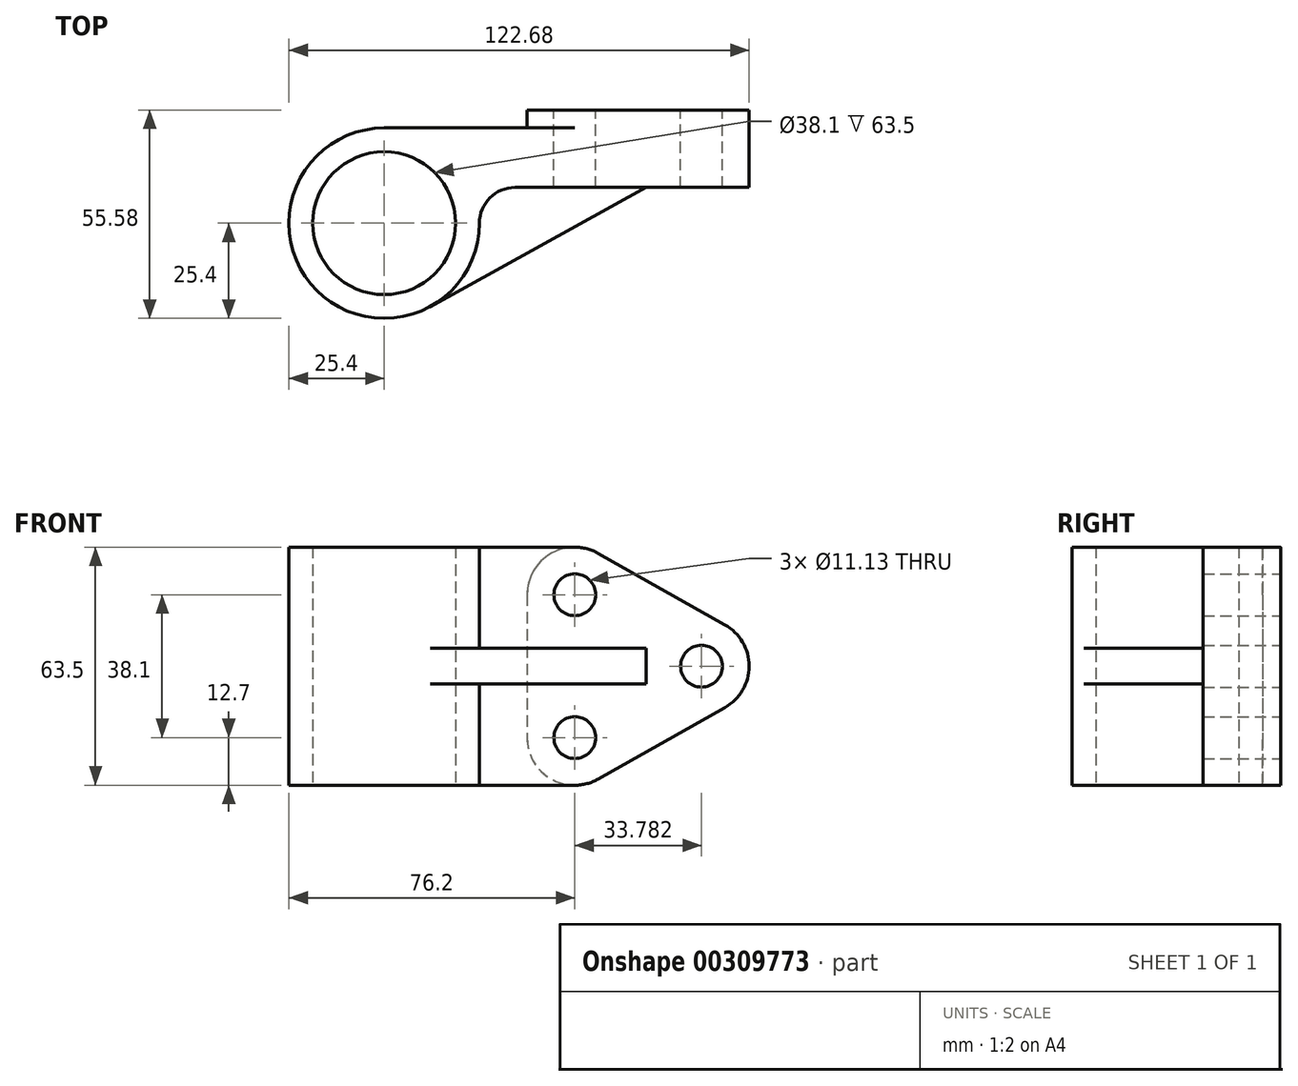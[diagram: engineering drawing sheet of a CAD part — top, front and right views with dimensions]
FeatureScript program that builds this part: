
annotation { "Feature Type Name" : "Feature", "Feature Type Description" : "" }
export const myFeature = defineFeature(function(context is Context, id is Id, definition is map)
    precondition{}
    {
        {
            var Q0;
            Q0=qCreatedBy(makeId("Top.planeOp"),FACE);
            var sketch = newSketch(context, id + "F0", { "sketchPlane" : qUnion([Q0])});
            skCircle(sketch, "E0", {"center": v(0, 0) * mm, "radius": 19.05 * mm});
            skLineSegment(sketch, "E1", {"start": v(0, 0) * mm, "end": v(25.4, 0) * mm});
            skLineSegment(sketch, "E2", {"start": v(34.92, 9.52) * mm, "end": v(84.58, 9.52) * mm});
            skLineSegment(sketch, "E3", {"start": v(0, 25.4) * mm, "end": v(50.8, 25.4) * mm});
            skLineSegment(sketch, "E4", {"start": v(50.8, 25.4) * mm, "end": v(50.8, 30.18) * mm});
            skLineSegment(sketch, "E5", {"start": v(50.8, 30.18) * mm, "end": v(84.58, 30.18) * mm});
            skLineSegment(sketch, "E6", {"start": v(84.58, 30.18) * mm, "end": v(84.58, 9.52) * mm});
            skArc(sketch, "E7", {"start": v(0, 25.4) * mm, "mid": v(-17.96, -17.96) * mm, "end": v(25.4, 0) * mm});
            skArc(sketch, "E8", {"start": v(34.92, 9.53) * mm, "mid": v(28.19, 6.74) * mm, "end": v(25.4, 0) * mm});
            skLineSegment(sketch, "E9", {"start": v(12.27, -22.24) * mm, "end": v(69.85, 9.52) * mm});
            skSolve(sketch);
        }
        {
            var Q0;
            Q0=makeQuery(id+"F0.imprint","IMPRINT",FACE,{"disambiguationData":[TD([[makeQuery(id+"F0.imprint","IMPRINT",EDGE,{"derivedFrom":sQuery(id+"F0.wireOp",EDGE,"E0")}),-1.0]])]});
            extrude(context, id + "F1", {"entities" : qUnion([Q0]), "endBound" : BoundingType.SYMMETRIC, "depth" : 63.5 * mm});
        }
        {
            var Q0;
            {var subQ0=sQuery(id+"F0.wireOp",EDGE,"E8");Q0=makeQuery(id+"F0.imprint","IMPRINT",FACE,{"disambiguationData":[TD([[makeQuery(id+"F0.imprint","IMPRINT",EDGE,{"derivedFrom":subQ0}),1.0]])]});}
            extrude(context, id + "F2", {"entities" : qUnion([Q0]), "operationType" : NewBodyOperationType.ADD, "endBound" : BoundingType.SYMMETRIC, "depth" : 9.52 * mm});
        }
        {
            var Q0;
            Q0=makeQuery(id+"F1.opExtrude","SWEPT_FACE",FACE,{"disambiguationData":[OSD([sQuery(id+"F0.wireOp",EDGE,"E5")])]});
            var sketch = newSketch(context, id + "F3", { "sketchPlane" : qUnion([Q0])});
            skSolve(sketch);
        }
        {
            var Q0;
            {var subQ0=sQuery(id+"F0.wireOp",EDGE,"E5");Q0=makeQuery(id+"F3.imprint","IMPRINT",FACE,{"disambiguationData":[TD([[makeQuery(id+"F3.imprint","IMPRINT",EDGE,{"derivedFrom":makeQuery(id+"F1.opExtrude","CAP_EDGE",EDGE,{"disambiguationData":[OSD([subQ0])],"isStart":true})}),-1.0]])]});}
            var sketch = newSketch(context, id + "F4", { "sketchPlane" : qUnion([Q0])});
            skCircle(sketch, "E10", {"center": v(-50.8, 19.05) * mm, "radius": 5.56 * mm});
            skCircle(sketch, "E11", {"center": v(-50.8, -19.05) * mm, "radius": 5.56 * mm});
            skCircle(sketch, "E12", {"center": v(-84.58, 0) * mm, "radius": 5.56 * mm});
            skLineSegment(sketch, "E13", {"start": v(-38.1, 19.05) * mm, "end": v(-38.1, -19.05) * mm});
            skArc(sketch, "E14", {"start": v(-38.1, 19.05) * mm, "mid": v(-44.4, 30.02) * mm, "end": v(-57.04, 30.11) * mm});
            skArc(sketch, "E15", {"start": v(-57.04, -30.11) * mm, "mid": v(-44.4, -30.02) * mm, "end": v(-38.1, -19.05) * mm});
            skLineSegment(sketch, "E16", {"start": v(-57.04, -30.11) * mm, "end": v(-90.82, -11.06) * mm});
            skLineSegment(sketch, "E17", {"start": v(-57.04, 30.11) * mm, "end": v(-90.82, 11.06) * mm});
            skArc(sketch, "E18", {"start": v(-90.82, 11.06) * mm, "mid": v(-97.28, 0) * mm, "end": v(-90.82, -11.06) * mm});
            skSolve(sketch);
        }
        {
            var Q0;
            Q0 = qSketchRegion(id + "F4", true);
            extrude(context, id + "F5", {"entities" : qUnion([Q0]), "operationType" : NewBodyOperationType.ADD, "oppositeDirection" : true, "depth" : 20.65 * mm});
        }
        {
            var Q0;
            {var subQ0=sQuery(id+"F4.wireOp",EDGE,"E11");var subQ1=makeQuery(id+"F3.imprint","IMPRINT",EDGE,{"derivedFrom":makeQuery(id+"F1.opExtrude","SWEPT_EDGE",EDGE,{"disambiguationData":[OSD([sQuery(id+"F0.wireOp",EDGE,"E4"),sQuery(id+"F0.wireOp",EDGE,"E5")])]})});var subQ2=makeQuery(id+"F4.imprint","INTERSECT",VERTEX,{"disambiguationData":[OD(0.0)],"derivedFrom":[subQ1,subQ0]});Q0=makeQuery(id+"F4.imprint","IMPRINT",FACE,{"disambiguationData":[TD([[makeQuery(id+"F4.imprint","IMPRINT",EDGE,{"disambiguationData":[TD([[subQ2,1.0]])],"derivedFrom":subQ0}),1.0]])]});}
            var Q1;
            {var subQ0=sQuery(id+"F4.wireOp",EDGE,"E10");var subQ1=makeQuery(id+"F3.imprint","IMPRINT",EDGE,{"derivedFrom":makeQuery(id+"F1.opExtrude","SWEPT_EDGE",EDGE,{"disambiguationData":[OSD([sQuery(id+"F0.wireOp",EDGE,"E4"),sQuery(id+"F0.wireOp",EDGE,"E5")])]})});var subQ2=makeQuery(id+"F4.imprint","INTERSECT",VERTEX,{"disambiguationData":[OD(0.0)],"derivedFrom":[subQ1,subQ0]});Q1=makeQuery(id+"F4.imprint","IMPRINT",FACE,{"disambiguationData":[TD([[makeQuery(id+"F4.imprint","IMPRINT",EDGE,{"disambiguationData":[TD([[subQ2,-1.0]])],"derivedFrom":subQ0}),1.0]])]});}
            var Q2;
            {var subQ0=sQuery(id+"F4.wireOp",EDGE,"E12");var subQ1=makeQuery(id+"F3.imprint","IMPRINT",EDGE,{"derivedFrom":makeQuery(id+"F1.opExtrude","SWEPT_EDGE",EDGE,{"disambiguationData":[OSD([sQuery(id+"F0.wireOp",EDGE,"E5"),sQuery(id+"F0.wireOp",EDGE,"E6")])]})});var subQ2=makeQuery(id+"F4.imprint","INTERSECT",VERTEX,{"disambiguationData":[OD(0.0)],"derivedFrom":[subQ1,subQ0]});Q2=makeQuery(id+"F4.imprint","IMPRINT",FACE,{"disambiguationData":[TD([[makeQuery(id+"F4.imprint","IMPRINT",EDGE,{"disambiguationData":[TD([[subQ2,-1.0]])],"derivedFrom":subQ0}),1.0]])]});}
            var Q3;
            {var subQ0=sQuery(id+"F4.wireOp",EDGE,"E10");var subQ1=makeQuery(id+"F3.imprint","IMPRINT",EDGE,{"derivedFrom":makeQuery(id+"F1.opExtrude","SWEPT_EDGE",EDGE,{"disambiguationData":[OSD([sQuery(id+"F0.wireOp",EDGE,"E4"),sQuery(id+"F0.wireOp",EDGE,"E5")])]})});var subQ2=makeQuery(id+"F4.imprint","INTERSECT",VERTEX,{"disambiguationData":[OD(0.0)],"derivedFrom":[subQ1,subQ0]});Q3=makeQuery(id+"F4.imprint","IMPRINT",FACE,{"disambiguationData":[TD([[makeQuery(id+"F4.imprint","IMPRINT",EDGE,{"disambiguationData":[TD([[subQ2,1.0]])],"derivedFrom":subQ0}),1.0]])]});}
            var Q4;
            {var subQ0=sQuery(id+"F4.wireOp",EDGE,"E11");var subQ1=makeQuery(id+"F3.imprint","IMPRINT",EDGE,{"derivedFrom":makeQuery(id+"F1.opExtrude","SWEPT_EDGE",EDGE,{"disambiguationData":[OSD([sQuery(id+"F0.wireOp",EDGE,"E4"),sQuery(id+"F0.wireOp",EDGE,"E5")])]})});var subQ2=makeQuery(id+"F4.imprint","INTERSECT",VERTEX,{"disambiguationData":[OD(0.0)],"derivedFrom":[subQ1,subQ0]});Q4=makeQuery(id+"F4.imprint","IMPRINT",FACE,{"disambiguationData":[TD([[makeQuery(id+"F4.imprint","IMPRINT",EDGE,{"disambiguationData":[TD([[subQ2,-1.0]])],"derivedFrom":subQ0}),1.0]])]});}
            var Q5;
            {var subQ1=sQuery(id+"F0.wireOp",EDGE,"E5");var subQ2=makeQuery(id+"F3.imprint","IMPRINT",EDGE,{"derivedFrom":makeQuery(id+"F1.opExtrude","CAP_EDGE",EDGE,{"disambiguationData":[OSD([subQ1])],"isStart":false})});Q5=makeQuery(id+"F4.imprint","IMPRINT",FACE,{"disambiguationData":[TD([[makeQuery(id+"F4.imprint","IMPRINT",EDGE,{"derivedFrom":subQ2}),1.0]])]});}
            var Q6;
            {var subQ1=sQuery(id+"F0.wireOp",EDGE,"E5");var subQ2=makeQuery(id+"F3.imprint","IMPRINT",EDGE,{"derivedFrom":makeQuery(id+"F1.opExtrude","CAP_EDGE",EDGE,{"disambiguationData":[OSD([subQ1])],"isStart":true})});Q6=makeQuery(id+"F4.imprint","IMPRINT",FACE,{"disambiguationData":[TD([[makeQuery(id+"F4.imprint","IMPRINT",EDGE,{"derivedFrom":subQ2}),-1.0]])]});}
            extrude(context, id + "F6", {"entities" : qUnion([Q0, Q1, Q2, Q3, Q4, Q5, Q6]), "operationType" : NewBodyOperationType.REMOVE, "endBound" : BoundingType.THROUGH_ALL, "oppositeDirection" : true, "depth" : 20.65 * mm});
        }
    });
